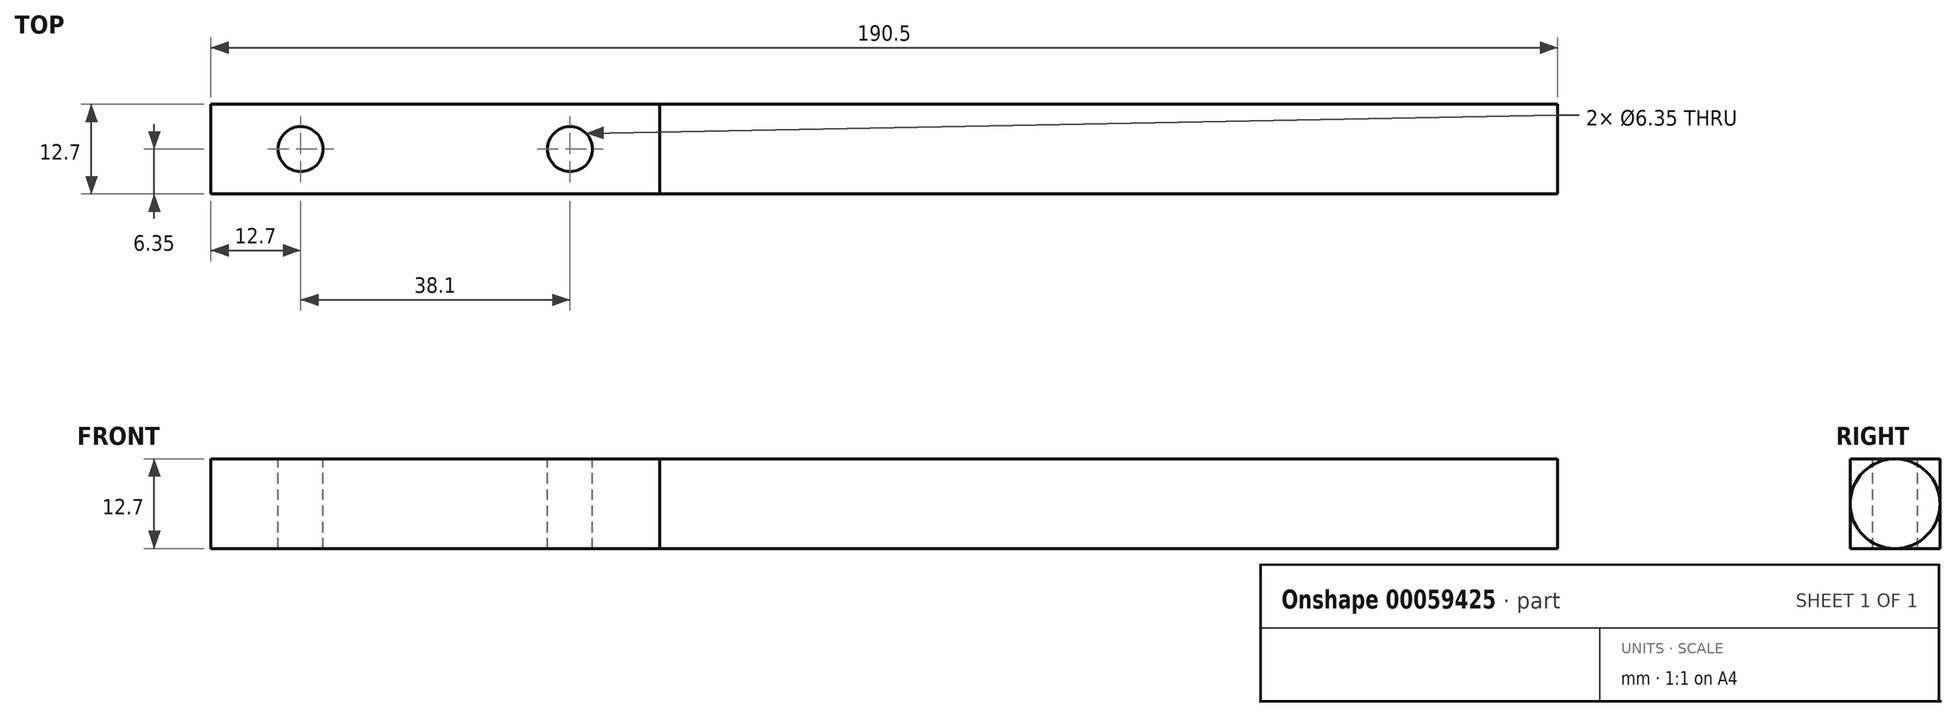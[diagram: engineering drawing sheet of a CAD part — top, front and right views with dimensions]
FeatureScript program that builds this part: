
annotation { "Feature Type Name" : "Feature", "Feature Type Description" : "" }
export const myFeature = defineFeature(function(context is Context, id is Id, definition is map)
    precondition{}
    {
        {
            var Q0;
            Q0=qCreatedBy(makeId("Right.planeOp"),FACE);
            var sketch = newSketch(context, id + "F0", { "sketchPlane" : qUnion([Q0])});
            skLineSegment(sketch, "E0.rect.bottom", {"start": v(6.35, -6.35) * mm, "end": v(-6.35, -6.35) * mm});
            skLineSegment(sketch, "E0.rect.top", {"start": v(6.35, 6.35) * mm, "end": v(-6.35, 6.35) * mm});
            skLineSegment(sketch, "E0.rect.left", {"start": v(6.35, -6.35) * mm, "end": v(6.35, 6.35) * mm});
            skLineSegment(sketch, "E0.rect.right", {"start": v(-6.35, -6.35) * mm, "end": v(-6.35, 6.35) * mm});
            skPoint(sketch, "E0.rect.middle", {"position": v(0, 0) * mm});
            skSolve(sketch);
        }
        {
            var Q0;
            Q0 = qSketchRegion(id + "F0", true);
            extrude(context, id + "F1", {"entities" : qUnion([Q0]), "depth" : 63.5 * mm});
        }
        {
            var Q0;
            Q0=makeQuery(id+"F1.opExtrude","CAP_FACE",FACE,{"disambiguationData":[OSD([sQuery(id+"F0.wireOp",EDGE,"E0.rect.bottom"),sQuery(id+"F0.wireOp",EDGE,"E0.rect.top"),sQuery(id+"F0.wireOp",EDGE,"E0.rect.left"),sQuery(id+"F0.wireOp",EDGE,"E0.rect.right")])],"isStart":false});
            var sketch = newSketch(context, id + "F2", { "sketchPlane" : qUnion([Q0])});
            skCircle(sketch, "E1", {"center": v(0, 0) * mm, "radius": 6.35 * mm});
            skSolve(sketch);
        }
        {
            var Q0;
            Q0 = qSketchRegion(id + "F2", true);
            extrude(context, id + "F3", {"entities" : qUnion([Q0]), "operationType" : NewBodyOperationType.ADD, "depth" : 127 * mm});
        }
        {
            var Q0;
            Q0=makeQuery(id+"F1.opExtrude","SWEPT_FACE",FACE,{"disambiguationData":[OSD([sQuery(id+"F0.wireOp",EDGE,"E0.rect.top")])]});
            var sketch = newSketch(context, id + "F4", { "sketchPlane" : qUnion([Q0])});
            skCircle(sketch, "E2", {"center": v(12.7, 0) * mm, "radius": 3.18 * mm});
            skCircle(sketch, "E3", {"center": v(50.8, 0) * mm, "radius": 3.18 * mm});
            skSolve(sketch);
        }
        {
            var Q0;
            Q0 = qSketchRegion(id + "F4", true);
            extrude(context, id + "F5", {"entities" : qUnion([Q0]), "operationType" : NewBodyOperationType.REMOVE, "endBound" : BoundingType.THROUGH_ALL, "oppositeDirection" : true, "depth" : 25.4 * mm});
        }
    });
